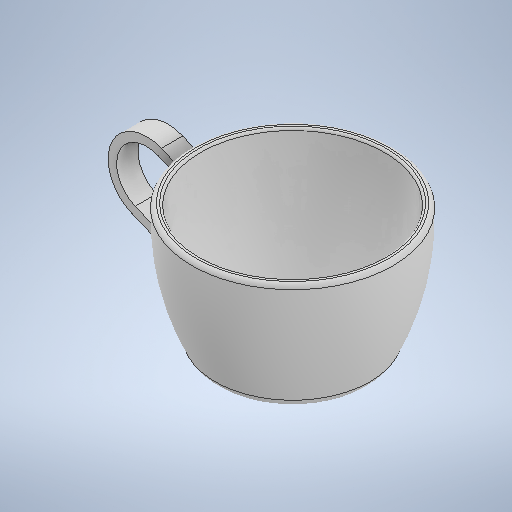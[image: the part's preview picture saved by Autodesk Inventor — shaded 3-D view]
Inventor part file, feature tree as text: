
AUTODESK INVENTOR PART (.ipt)
format: ipt  version: 2025.2 (Build 292293000, 293)  size: 327,168 bytes
history: native  units: in
note: dims shown in document units (in); Inventor stores cm internally (conversion verified against a paired STEP export)
features: sketch x2, revolve x1, extrude x1
ambient origin geometry x8: Origin, YZ Plane, XZ Plane, XY Plane, X Axis, Y Axis, Z Axis, Center Point
bodies: Solid1 (feature_tree)
feature tree (4):
  revolve  "Revolution1"  [1 undecoded]
  extrude  "Extrusion1"  Depth=0.0394in
  sketch  "Sketch1"  dims[d6=0.6102in d9=2.2047in]
  sketch  "Sketch2"  dims[d10=0.0787in d11=0.0394in d12=0.0394in d13=0.0394in d14=0.1969in d15=360.0deg d19=0.0787in d20=0.1969in d21=0.0in]
note: 1 required parameter value undecoded (feature->parameter linkage not recoverable at this tier; creation-order binding heuristic only, values carry confidence <= 0.55)
